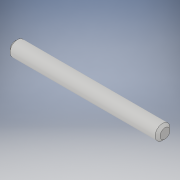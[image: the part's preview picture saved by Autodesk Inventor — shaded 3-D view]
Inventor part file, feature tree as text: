
AUTODESK INVENTOR PART (.ipt)
format: ipt  version: 2018.3 (Build 223284000, 284)  size: 97,792 bytes
history: native  units: in
note: dims shown in document units (in); Inventor stores cm internally (conversion verified against a paired STEP export)
features: revolve x1, chamfer x1, sketch x1
ambient origin geometry x8: Origin, YZ Plane, XZ Plane, XY Plane, X Axis, Y Axis, Z Axis, Center Point
bodies: Solid1 (feature_tree)
feature tree (3):
  revolve  "Revolution1"  [1 undecoded]
  chamfer  "Chamfer1"  Angle=90.0deg  [1 undecoded]
  sketch  "Sketch1"  dims[d0=0.61in d1=0.0301in d2=90.0deg d3=0.01in d4=0.125in d5=45.0deg]
note: 2 required parameter values undecoded (feature->parameter linkage not recoverable at this tier; creation-order binding heuristic only, values carry confidence <= 0.55)